# Revit family: Transom with Trim
name_source: partatom
category: Windows
revit_build: Autodesk Revit Architecture 2012 (Build: 20110210_1515)
units: mm (PartAtom-declared; Revit-internal decimal feet)

## types (10) — shared parameters
Assembly Code = B2020100
Default Sill Height = 7' - 1"
Trim Projection - Ext. = 0' - 0 1/2"
Trim Projection - Int. = 0' - 0 3/4"
Trim Width - Exterior = 0' - 3 1/2"
Trim Width - Interior = 0' - 3 1/2"
Wall Closure = By host
Window Inset = 0' - 0 3/4"

## per-type parameters (varying)
| type | Glass Pane Material | Height | Sash Material | Trim Exterior Material | Trim Interior Material | Width |
| 24" x 24" | Glass | 2' - 0" | Sash | Trim | Trim | 2' - 0" |
| 36" x 24" | Glass | 2' - 0" | Sash | Trim | Trim | 3' - 0" |
| 48" x 24" | Glass | 2' - 0" | Sash | Trim | Trim | 4' - 0" |
| 60" x 24" | <By Category> | 2' - 0" | <By Category> | <By Category> | <By Category> | 5' - 0" |
| 72" x 24" | Glass | 2' - 0" | Sash | Trim | Trim | 6' - 0" |
| 24" x 18" | Glass | 1' - 6" | Sash | Trim | Trim | 2' - 0" |
| 36" x 18" | Glass | 1' - 6" | Sash | Trim | Trim | 3' - 0" |
| 48" x 18" | Glass | 1' - 6" | Sash | Trim | Trim | 4' - 0" |
| 60" x 18" | Glass | 1' - 6" | Sash | Trim | Trim | 5' - 0" |
| 72" x 18" | Glass | 1' - 6" | Sash | Trim | Trim | 6' - 0" |
